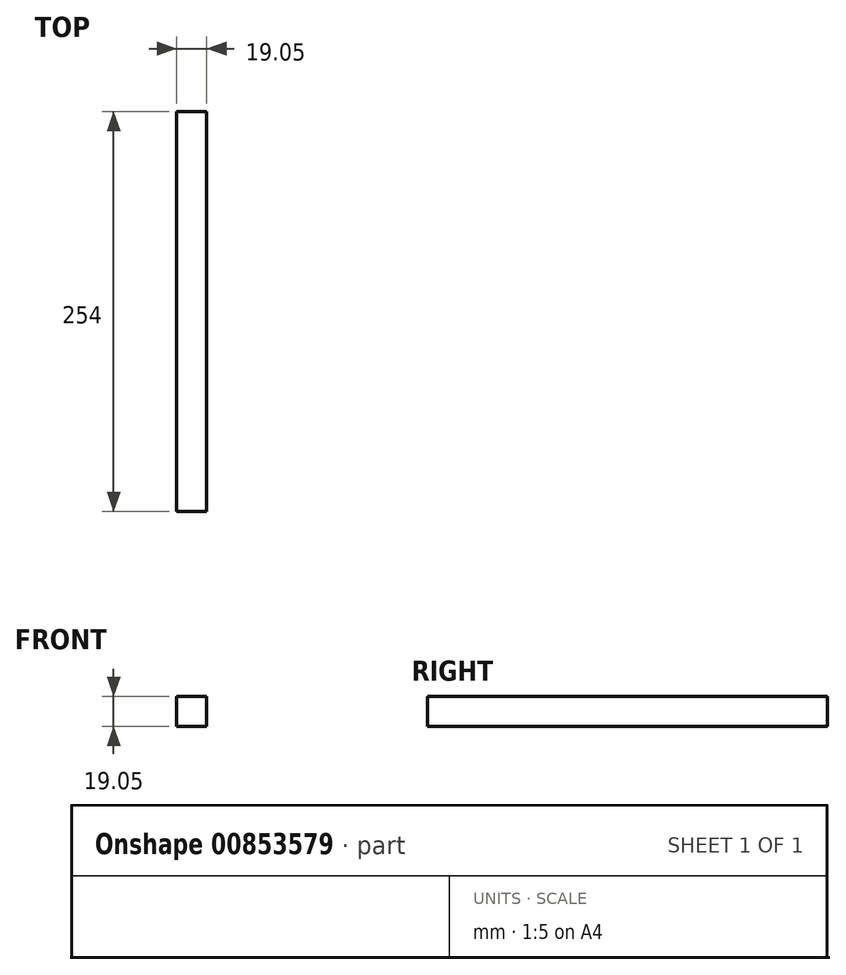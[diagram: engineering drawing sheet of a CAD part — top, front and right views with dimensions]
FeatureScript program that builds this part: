
annotation { "Feature Type Name" : "Feature", "Feature Type Description" : "" }
export const myFeature = defineFeature(function(context is Context, id is Id, definition is map)
    precondition{}
    {
        {
            var Q0;
            Q0=qCreatedBy(makeId("Front.planeOp"),FACE);
            var sketch = newSketch(context, id + "F0", { "sketchPlane" : qUnion([Q0])});
            skLineSegment(sketch, "E0.bottom", {"start": v(0, 0) * mm, "end": v(19.05, 0) * mm});
            skLineSegment(sketch, "E0.top", {"start": v(0, 19.05) * mm, "end": v(19.05, 19.05) * mm});
            skLineSegment(sketch, "E0.left", {"start": v(0, 0) * mm, "end": v(0, 19.05) * mm});
            skLineSegment(sketch, "E0.right", {"start": v(19.05, 0) * mm, "end": v(19.05, 19.05) * mm});
            skSolve(sketch);
        }
        {
            var Q0;
            Q0 = qSketchRegion(id + "F0", true);
            extrude(context, id + "F1", {"entities" : qUnion([Q0]), "depth" : 254 * mm, "offsetDistance" : 25.4 * mm});
        }
    });
